# Revit family: IS_Tesi_T4932_BIM_NL
name_source: partatom
category: Plumbing Fixtures
units: mm (PartAtom-declared; Revit-internal decimal feet)

## family parameters
Always vertical = No
Cut with Voids When Loaded = No
OmniClass Number = 23.45.05.21.11.11
OmniClass Title = Water Operated Water Closets
Part Type = Normal
Room Calculation Point = No
Round Connector Dimension = Use Diameter
Shared = No
Work Plane-Based = No

## types (4) — shared parameters
Afmetingen = 340 x 530 x 360 mm
AfstandsEenheid = Millimeter
Auteur = Ideal Standard
BIMobject category = Toilets
BIMobject category code = toilets
BIMobject main category = Sanitary
BIMobject main category code = sanitary
Beschrijvinggarantie = Herstellergarantie
BimObjectNaam = IS_IdealStandard_WCpans_Tesi_T4932_IdealStandard
Brand url = https://www.idealstandard.nl
Breedte = 360.248236
Date of publishing = 15/03/2023
Diepte = 530 mm
DuurEenheid = Jahre
Edition number = 1
Garantieonderdelen = https://www.idealstandard.nl
Garantieunits = Jahre
GemaaktOp = 15/03/2023
Hoogte = 339,133197784424
Hulp = https://www.idealstandard.nl
IFC Classification = Sanitary Terminal
IfcExportAs = IfcSanitaryTerminalType
IfcExportType = TOILETPAN
Installatieinstructies = https://www.idealstandard.nl
Installation instructions = https://www.idealstandard.nl
Lengte = 530 mm
Manufacturer = Ideal Standard
Manufacturer name = Ideal Standard
Masterformat 2014 Code = 10 28 13
Masterformat 2014 Description = Toilet Accessories
Materiaal = Ceramics
MateriaalWC = Ceramics
Material main = Ceramics
Merk = Ideal Standard
Montageinstuctie = https://www.idealstandard.nl
NBS Reference Code = 45-35-70/384
NBS Reference Description = WC pans
Nettogewicht = 21.6
NominalHeight = 339 mm
NominalLength = 530 mm
NominalWidth = 360 mm
OmniClass Code = 23-31 19 00
OmniClass Description = Toilets
OppervlakteEenheid = Millimeter
Product Guid = 94668fd0-2334-444d-bdbb-285528e3b5e8
Product SKU = T4932
Product certification = https://www.idealstandard.nl
Product data url = https://bimobject.com
Product family = TESI
Product group = Tesi
Product name = Tesi wh bowl RimLS
Product url = https://www.idealstandard.nl
Productinformatie = https://www.idealstandard.nl
QR code = http://bimobject.com
Revisie = 1
Size = 340 x 530 x 360 mm
Technical description = https://www.idealstandard.nl
Telefoonnummer = 077 355 08 08
Toepassing = WC Pans
TypeWC = Wand aufgehängt
Typeconnectie = Installation
TypespoelingWC = afspoelen
UNSPSC Code = 301815
URL = https://www.idealstandard.nl
Uniclass 2015 Code = Pr_40_20_93_94
Uniclass 2015 Name = WC pans
Uniclass2015Beschrijving = WC pans
Uniclass2015Referentie = Pr_40_20_93_94
Uniclass2015Version = v1.26
Uniformat II Code = D2010
Uniformat II Description = Plumbing Fixtures
Urlproducent = https://www.idealstandard.nl
ValutaEenheid = Euro
Versie = 1
Verwachtelevensduur = 99
Volumeunits = Liter
Vorm = geformt
Wisselstukken = https://www.idealstandard.nl
Youtube clip = https://www.youtube.com
zero-valued in all types: BrutoGewicht, Cost, Default Elevation, Vervangingskosten

## per-type parameters (varying)
| type | Afwerking | Artikelnummer | Artikelomschrijving | Artikelreferentie | Barcode | Description | Eigenschappen | GTIN code | Kleur | Kleurwc | Model | Referentie |
| T493201 - Tesi wall mounted bowl RimLS+ EASY FIX+ in carton box, in white | Weiß | T493201 | Ideal Standard Tesi Wandtiefspül-WC RimLS+ EASY FIX+ in Kartonverpackung, in Weiß | T493201 | 8014140509622 | Tesi Wandtiefspül-WC RimLS+ EASY FIX+ in Kartonverpackung, in Weiß | Wandtiefspül-WC RimLS+ EASY FIX+ in Kartonverpackung, in Weiß | 8014140509622 | Weiß | Weiß | T493201 | Ideal Standard Tesi Wandtiefspül-WC RimLS+ EASY FIX+ in Kartonverpackung, in Weiß |
| T4932MA - Tesi wall mounted bowl RimLS+ EASY FIX+ in carton box, IDEAL PLUS finish | Weiß Ideal Plus | T4932MA | Ideal Standard Tesi Wandtiefspül-WC RimLS+ EASY FIX+ in Kartonverpackung, mit IDEAL PLUS Oberfläche | T4932MA | 8014140511465 | Tesi Wandtiefspül-WC RimLS+ EASY FIX+ in Kartonverpackung, mit IDEAL PLUS Oberfläche | Wandtiefspül-WC RimLS+ EASY FIX+ in Kartonverpackung, mit IDEAL PLUS Oberfläche | 8014140511465 | Weiß Ideal Plus | Weiß Ideal Plus | T4932MA | Ideal Standard Tesi Wandtiefspül-WC RimLS+ EASY FIX+ in Kartonverpackung, mit IDEAL PLUS Oberfläche |
| T4932V1 - Tesi wall mounted bowl RimLS+ EASY FIX+ in carton box, in SILK WHITE | Seidenweiß | T4932V1 | Ideal Standard Tesi Wandtiefspül-WC RimLS+ EASY FIX+ in Kartonverpackung, in Seidenweiß | T4932V1 | 8014140515074 | Tesi Wandtiefspül-WC RimLS+ EASY FIX+ in Kartonverpackung, in Seidenweiß | Wandtiefspül-WC RimLS+ EASY FIX+ in Kartonverpackung, in Seidenweiß | 8014140515074 | Seidenweiß | Seidenweiß | T4932V1 | Ideal Standard Tesi Wandtiefspül-WC RimLS+ EASY FIX+ in Kartonverpackung, in Seidenweiß |
| T4932V3 - Tesi wall mounted bowl RimLS+ EASY FIX+ in carton box, in SILK BLACK | Seidenschwarz | T4932V3 | Ideal Standard Tesi Wandtiefspül-WC RimLS+ EASY FIX+ in Kartonverpackung, in Seidenschwarz | T4932V3 | 8014140511472 | Tesi Wandtiefspül-WC RimLS+ EASY FIX+ in Kartonverpackung, in Seidenschwarz | Wandtiefspül-WC RimLS+ EASY FIX+ in Kartonverpackung, in Seidenschwarz | 8014140511472 | Seidenschwarz | Seidenschwarz | T4932V3 | Ideal Standard Tesi Wandtiefspül-WC RimLS+ EASY FIX+ in Kartonverpackung, in Seidenschwarz |

## geometry (parser evidence)
native form markers: Blend x4, Sweep x3
no freeform markers — native parametric forms only
